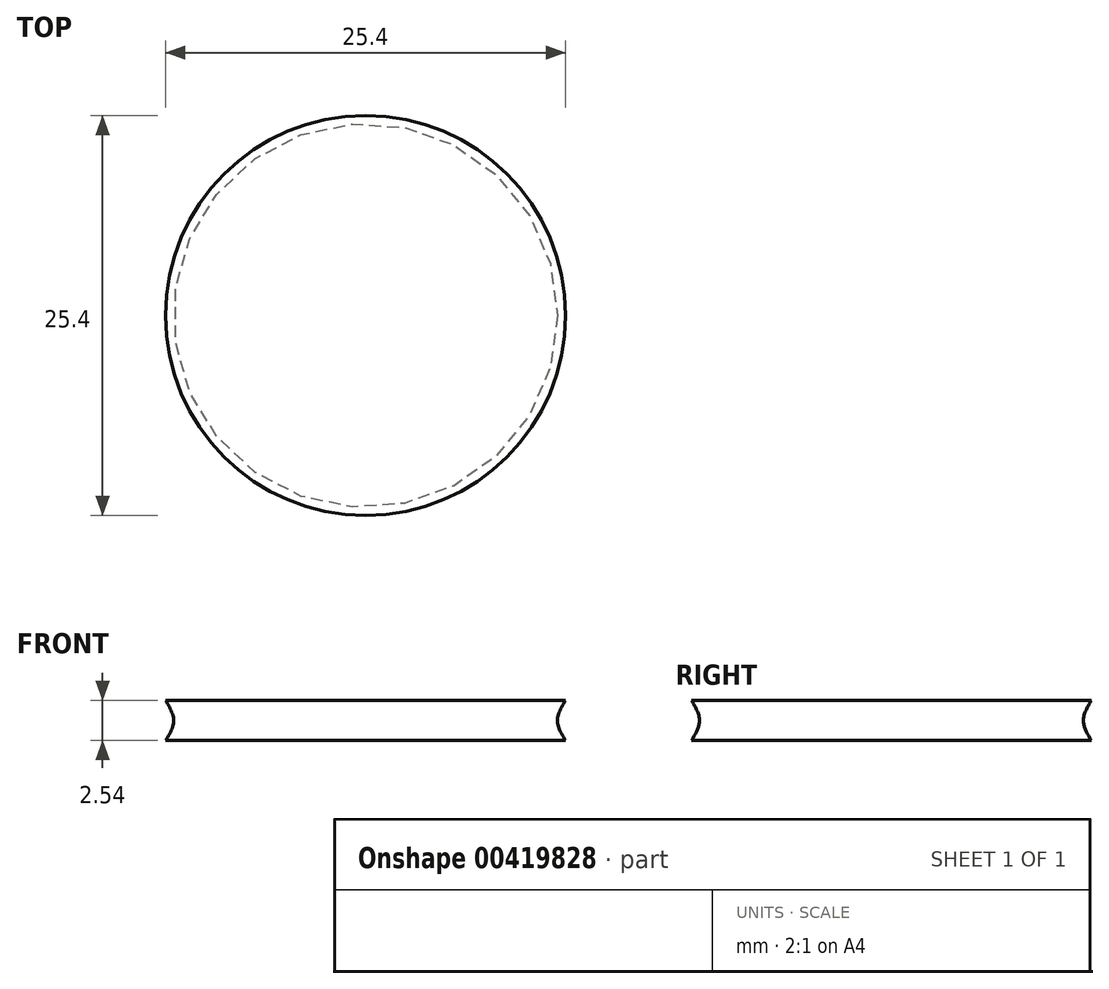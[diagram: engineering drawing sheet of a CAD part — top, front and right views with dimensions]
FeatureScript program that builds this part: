
annotation { "Feature Type Name" : "Feature", "Feature Type Description" : "" }
export const myFeature = defineFeature(function(context is Context, id is Id, definition is map)
    precondition{}
    {
        {
            var Q0;
            Q0=qCreatedBy(makeId("Front.planeOp"),FACE);
            var sketch = newSketch(context, id + "F0", { "sketchPlane" : qUnion([Q0])});
            skLineSegment(sketch, "E0", {"start": v(0, 1.27) * mm, "end": v(12.7, 1.27) * mm});
            skLineSegment(sketch, "E1", {"start": v(0, -1.27) * mm, "end": v(12.7, -1.27) * mm});
            skFitSpline(sketch, "E2", {"points": [v(12.7, 1.27) * mm, v(12.2, 0) * mm, v(12.7, -1.27) * mm], "startDerivative": vector(-1.52, -2.58) * mm, "endDerivative": vector(1.66, -2.5) * mm});
            skLineSegment(sketch, "E3", {"start": v(0, 1.27) * mm, "end": v(0, -1.27) * mm});
            skSolve(sketch);
        }
        {
            var Q0;
            Q0=qSketchRegion(id+"F0",true);
            var Q1;
            Q1=sQuery(id+"F0.wireOp",EDGE,"E3");
            revolve(context, id + "F1", {"entities" : qUnion([Q0]), "axis" : qUnion([Q1]), "revolveType" : RevolveType.FULL});
        }
    });
